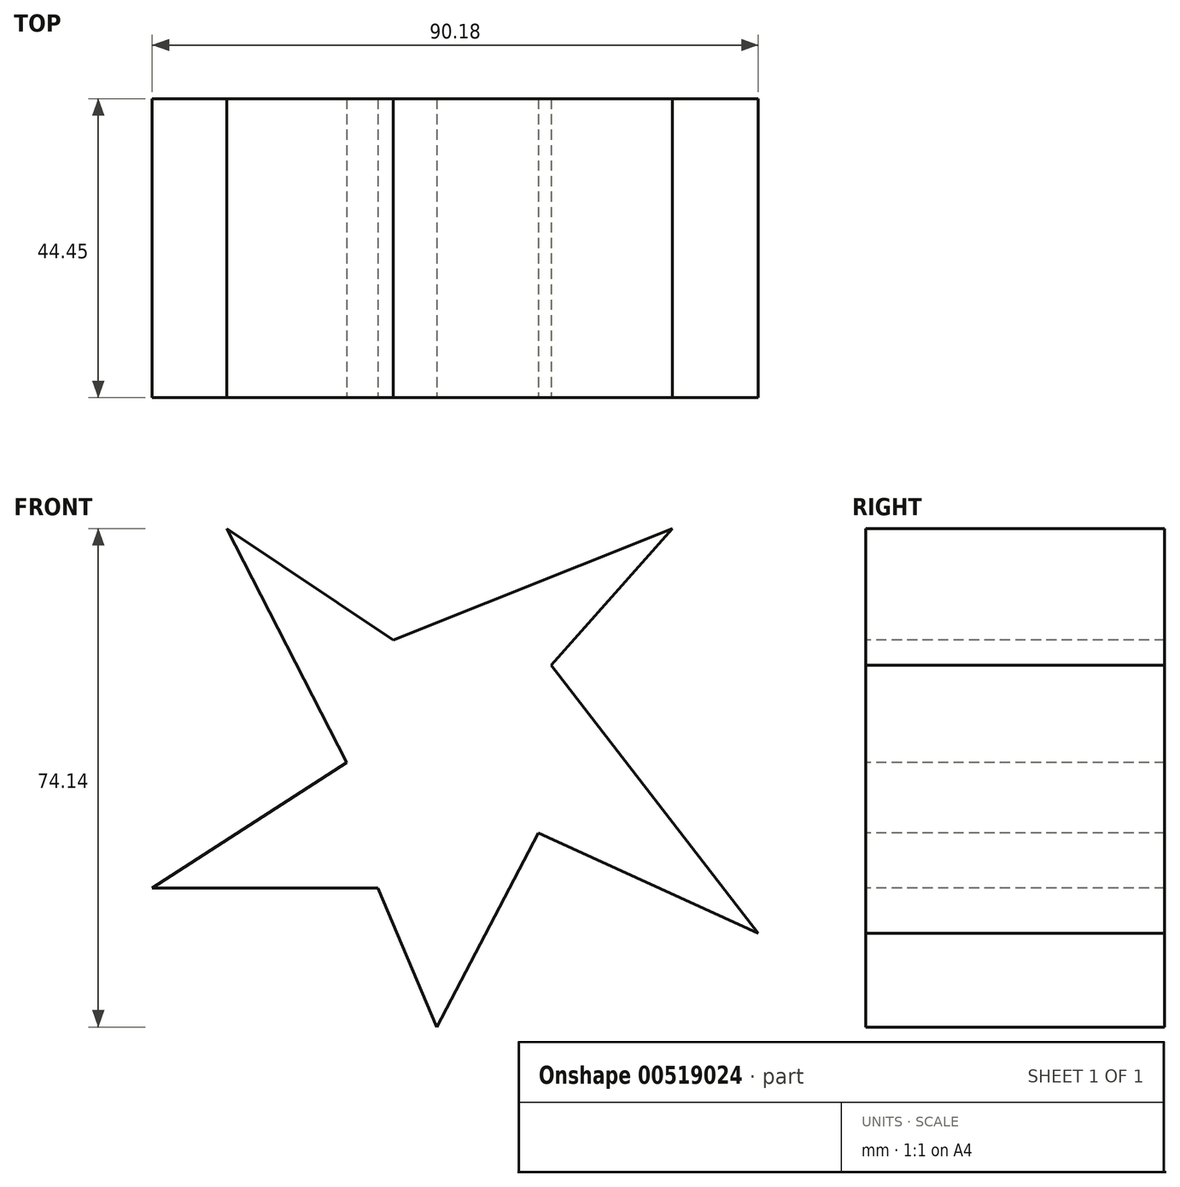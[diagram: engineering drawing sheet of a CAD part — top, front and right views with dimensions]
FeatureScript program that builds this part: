
annotation { "Feature Type Name" : "Feature", "Feature Type Description" : "" }
export const myFeature = defineFeature(function(context is Context, id is Id, definition is map)
    precondition{}
    {
        {
            var Q0;
            Q0=qCreatedBy(makeId("Front.planeOp"),FACE);
            var sketch = newSketch(context, id + "F0", { "sketchPlane" : qUnion([Q0])});
            skLineSegment(sketch, "E0", {"start": v(0, 0) * mm, "end": v(15.1, 28.84) * mm});
            skLineSegment(sketch, "E1", {"start": v(15.1, 28.84) * mm, "end": v(47.82, 13.95) * mm});
            skLineSegment(sketch, "E2", {"start": v(47.82, 13.95) * mm, "end": v(16.99, 53.8) * mm});
            skLineSegment(sketch, "E3", {"start": v(16.99, 53.8) * mm, "end": v(35.02, 74.14) * mm});
            skLineSegment(sketch, "E4", {"start": v(35.02, 74.14) * mm, "end": v(-6.5, 57.57) * mm});
            skLineSegment(sketch, "E5", {"start": v(-6.5, 57.57) * mm, "end": v(-31.25, 74.14) * mm});
            skLineSegment(sketch, "E6", {"start": v(-31.25, 74.14) * mm, "end": v(-13.42, 39.32) * mm});
            skLineSegment(sketch, "E7", {"start": v(-13.42, 39.32) * mm, "end": v(-42.36, 20.66) * mm});
            skLineSegment(sketch, "E8", {"start": v(-42.36, 20.66) * mm, "end": v(-8.8, 20.66) * mm});
            skLineSegment(sketch, "E9", {"start": v(-8.8, 20.66) * mm, "end": v(0, 0) * mm});
            skSolve(sketch);
        }
        {
            var Q0;
            Q0=makeQuery(id+"F0.imprint","IMPRINT",FACE,{"disambiguationData":[TD([[makeQuery(id+"F0.imprint","IMPRINT",EDGE,{"derivedFrom":sQuery(id+"F0.wireOp",EDGE,"E0")}),1.0]])]});
            extrude(context, id + "F1", {"entities" : qUnion([Q0]), "oppositeDirection" : true, "depth" : 44.45 * mm, "offsetDistance" : 25.4 * mm});
        }
    });
